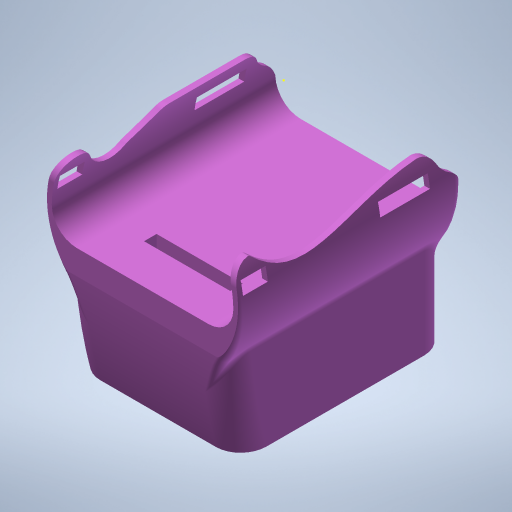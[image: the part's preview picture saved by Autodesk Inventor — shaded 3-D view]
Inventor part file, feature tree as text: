
AUTODESK INVENTOR PART (.ipt)
format: ipt  version: 2024 (Build 280153000, 153)  size: 749,568 bytes
history: native  units: mm
features: sketch x14, extrude x11, fillet x8, plane x3, projected_geometry x2, split x1, other x1
ambient origin geometry x8: Origin, YZ Plane, XZ Plane, XY Plane, X Axis, Y Axis, Z Axis, Center Point
bodies: Solid1 (feature_tree)
feature tree (40):
  extrude  "Extrusion1"  Depth=77.5mm
  extrude  "Extrusion2"  Depth=15.0mm
  sketch  "Sketch3"  dims[d5=90.0mm d6=0.0mm d7=60.0mm d8=0.0mm d9=50.0mm d11=80.0mm d12=90.0mm d13=0.0mm d14=10.0mm]
  extrude  "Extrusion3"  Depth=60.0mm TaperAngle=0.0deg
  fillet  "Fillet1"  Radius=50.0mm
  fillet  "Fillet2"  Radius=80.0mm
  fillet  "Fillet3"  Radius=90.0mm
  fillet  "Fillet4"  Radius=10.0mm
  plane  "Work Plane1"
  extrude  "Extrusion4"  Depth=3.0mm
  extrude  "Extrusion5"  [1 undecoded]
  fillet  "Fillet5"  Radius=20.0mm
  fillet  "Fillet6"  Radius=20.0mm
  plane  "Work Plane2"
  extrude  "Extrusion6"  Depth=20.0mm
  fillet  "Fillet7"  Radius=50.0mm
  plane  "Work Plane3"
  split  "Split1"
  sketch  "Sketch8"  dims[d28=81.25mm d29=10.0mm d30=0.0mm]
  extrude  "Extrusion7"  Depth=7.0mm
  extrude  "Extrusion8"  Depth=10.0mm TaperAngle=0.0deg
  extrude  "Extrusion10"  [1 undecoded]
  extrude  "Extrusion11"  Depth=5.0mm
  sketch  "Sketch14"  dims[d48=52.0mm d49=0.0mm]
  extrude  "Extrusion12"  Depth=5.0mm
  other  "Lip1"
  fillet  "Fillet12"  Radius=20.0mm
  sketch  "Sketch1"  dims[d0=73.0mm d1=77.5mm]
  sketch  "Sketch2"  dims[d3=10.0mm d4=15.0mm]
  projected_geometry  "Projected Loop1"
  sketch  "Sketch4"  dims[d15=5.0mm d16=3.0mm]
  sketch  "Sketch5"  dims[d17=10.0mm d18=-39.5mm d19=20.0mm d20=20.0mm]
  sketch  "Sketch6"  dims[d21=50.0mm d22=0.0mm d23=20.0mm d24=50.0mm d25=0.0mm]
  sketch  "Sketch7"  dims[d26=10.0mm d27=7.0mm]
  projected_geometry  "Projected Loop2"
  sketch  "Sketch9"  dims[d31=1.0mm d32=-60.75mm]
  sketch  "Sketch10"  dims[d33=10.0mm d34=0.0mm d38=5.0mm]
  sketch  "Sketch12"  dims[d39=10.0mm d40=5.0mm d41=20.0mm]
  sketch  "Sketch13"  dims[d42=10.0mm d43=0.0mm]
  sketch  "Sketch15"  dims[d50=8.0mm d51=8.0mm d52=19.25mm d53=0.0mm d55=30.0mm d56=0.0mm d57=1.0mm d58=1.0mm d59=0.0mm d60=0.0mm d61=0.0mm d62=0.0mm d64=5.0mm d46=0.5mm d47=0.872665mm]
note: 2 required parameter values undecoded (feature->parameter linkage not recoverable at this tier; creation-order binding heuristic only, values carry confidence <= 0.55)
